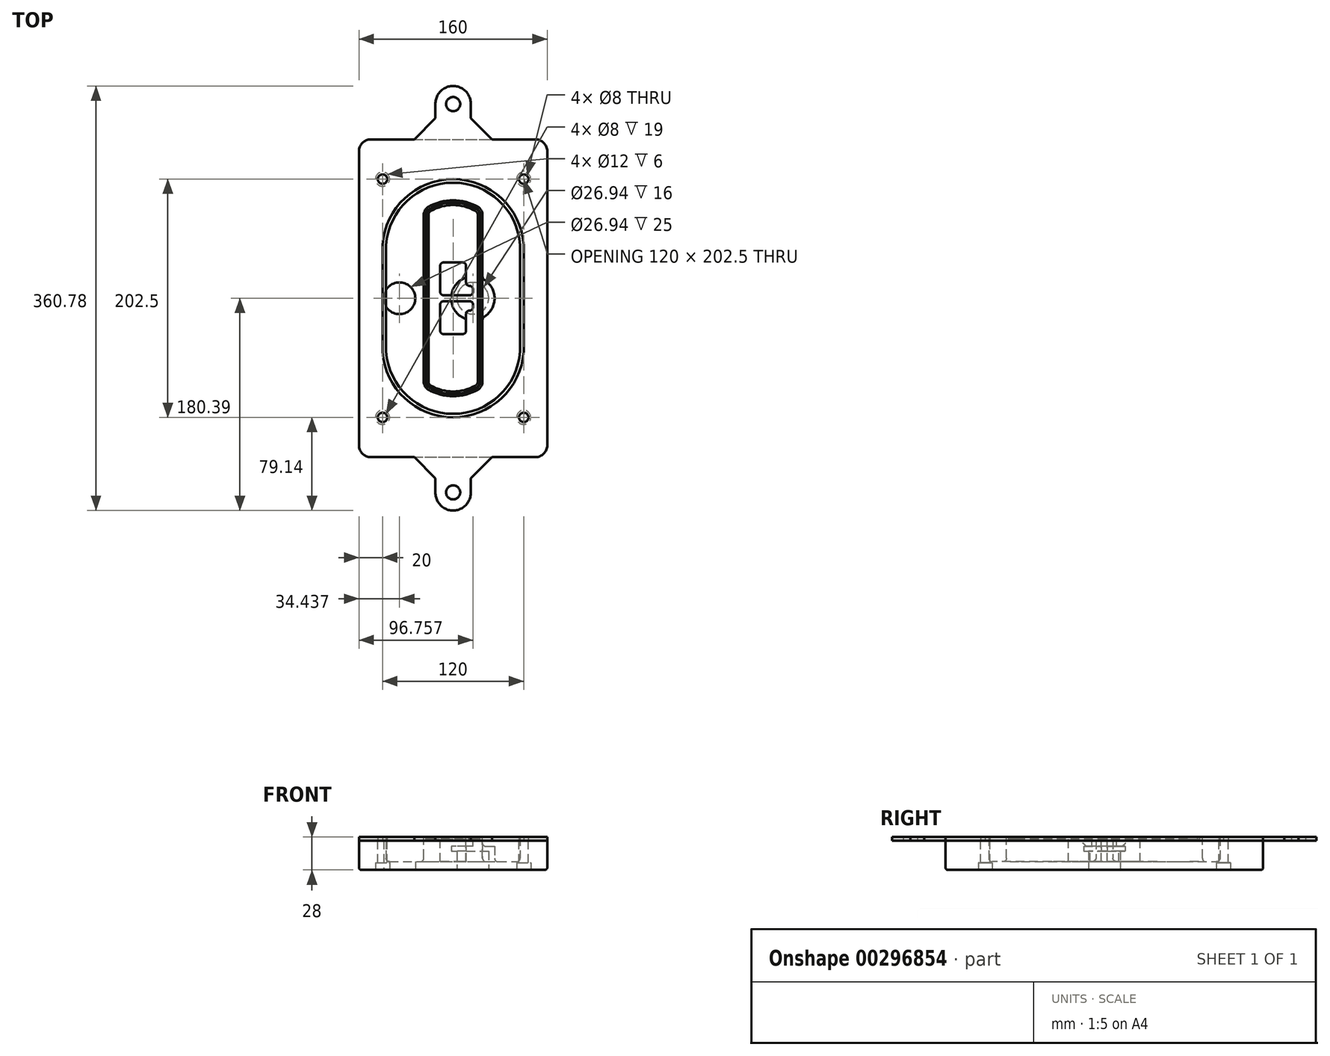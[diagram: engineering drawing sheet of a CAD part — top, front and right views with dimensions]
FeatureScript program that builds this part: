
annotation { "Feature Type Name" : "Feature", "Feature Type Description" : "" }
export const myFeature = defineFeature(function(context is Context, id is Id, definition is map)
    precondition{}
    {
        {
            var Q0;
            Q0=qCreatedBy(makeId("Top.planeOp"),FACE);
            var sketch = newSketch(context, id + "F0", { "sketchPlane" : qUnion([Q0])});
            skPoint(sketch, "E0.rect.middle", {"position": v(0, 0) * mm});
            skLineSegment(sketch, "E1.bottom", {"start": v(-70, -135) * mm, "end": v(70, -135) * mm});
            skLineSegment(sketch, "E1.top", {"start": v(-70, 135) * mm, "end": v(70, 135) * mm});
            skLineSegment(sketch, "E1.left", {"start": v(-80, -125) * mm, "end": v(-80, 125) * mm});
            skLineSegment(sketch, "E1.right", {"start": v(80, -125) * mm, "end": v(80, 125) * mm});
            skLineSegment(sketch, "E2", {"start": v(-80, 135) * mm, "end": v(80, -135) * mm, "construction": true});
            skLineSegment(sketch, "E3", {"start": v(80, 135) * mm, "end": v(-80, -135) * mm, "construction": true});
            skCircle(sketch, "E4", {"center": v(-60, 101.25) * mm, "radius": 4 * mm});
            skCircle(sketch, "E5", {"center": v(60, 101.25) * mm, "radius": 4 * mm});
            skCircle(sketch, "E6", {"center": v(60, -101.25) * mm, "radius": 4 * mm});
            skCircle(sketch, "E7", {"center": v(-60, -101.25) * mm, "radius": 4 * mm});
            skLineSegment(sketch, "E8", {"start": v(-60, 101.25) * mm, "end": v(60, 101.25) * mm, "construction": true});
            skLineSegment(sketch, "E9", {"start": v(60, 101.25) * mm, "end": v(60, -101.25) * mm, "construction": true});
            skLineSegment(sketch, "E10", {"start": v(60, -101.25) * mm, "end": v(-60, -101.25) * mm, "construction": true});
            skLineSegment(sketch, "E11", {"start": v(-60, -101.25) * mm, "end": v(-60, 101.25) * mm, "construction": true});
            skLineSegment(sketch, "E12", {"start": v(-60, 44.66) * mm, "end": v(-60, -44.66) * mm});
            skLineSegment(sketch, "E13", {"start": v(60, 44.66) * mm, "end": v(60, -44.66) * mm});
            skArc(sketch, "E14", {"start": v(59.98, 45.37) * mm, "mid": v(0, 101.25) * mm, "end": v(-59.98, 45.37) * mm});
            skArc(sketch, "E15", {"start": v(-59.98, -45.37) * mm, "mid": v(0, -101.25) * mm, "end": v(59.98, -45.37) * mm});
            skLineSegment(sketch, "E16", {"start": v(-60, 0) * mm, "end": v(60, 0) * mm, "construction": true});
            skPoint(sketch, "E17.visualSharp", {"position": v(-60, -45) * mm});
            skArc(sketch, "E17.filletArc", {"start": v(-60, -44.66) * mm, "mid": v(-60, -45.02) * mm, "end": v(-59.98, -45.37) * mm});
            skPoint(sketch, "E18.visualSharp", {"position": v(-60, 45) * mm});
            skArc(sketch, "E18.filletArc", {"start": v(-59.98, 45.37) * mm, "mid": v(-60, 45.02) * mm, "end": v(-60, 44.66) * mm});
            skPoint(sketch, "E19.visualSharp", {"position": v(60, 45) * mm});
            skArc(sketch, "E19.filletArc", {"start": v(60, 44.66) * mm, "mid": v(60, 45.02) * mm, "end": v(59.98, 45.37) * mm});
            skPoint(sketch, "E20.visualSharp", {"position": v(60, -45) * mm});
            skArc(sketch, "E20.filletArc", {"start": v(59.98, -45.37) * mm, "mid": v(60, -45.02) * mm, "end": v(60, -44.66) * mm});
            skPoint(sketch, "E21.visualSharp", {"position": v(-80, 135) * mm});
            skArc(sketch, "E21.filletArc", {"start": v(-70, 135) * mm, "mid": v(-77.07, 132.07) * mm, "end": v(-80, 125) * mm});
            skPoint(sketch, "E22.visualSharp", {"position": v(80, 135) * mm});
            skArc(sketch, "E22.filletArc", {"start": v(80, 125) * mm, "mid": v(77.07, 132.07) * mm, "end": v(70, 135) * mm});
            skPoint(sketch, "E23.visualSharp", {"position": v(80, -135) * mm});
            skArc(sketch, "E23.filletArc", {"start": v(70, -135) * mm, "mid": v(77.07, -132.07) * mm, "end": v(80, -125) * mm});
            skPoint(sketch, "E24.visualSharp", {"position": v(-80, -135) * mm});
            skArc(sketch, "E24.filletArc", {"start": v(-80, -125) * mm, "mid": v(-77.07, -132.07) * mm, "end": v(-70, -135) * mm});
            skArc(sketch, "E25.0", {"start": v(57, 44.66) * mm, "mid": v(57, 44.9) * mm, "end": v(56.98, 45.16) * mm});
            skLineSegment(sketch, "E25.1", {"start": v(57, 44.66) * mm, "end": v(57, -44.66) * mm});
            skArc(sketch, "E25.2", {"start": v(56.98, -45.16) * mm, "mid": v(57, -44.9) * mm, "end": v(57, -44.66) * mm});
            skArc(sketch, "E25.3", {"start": v(-56.98, -45.16) * mm, "mid": v(0, -98.25) * mm, "end": v(56.98, -45.16) * mm});
            skArc(sketch, "E25.4", {"start": v(-57, -44.66) * mm, "mid": v(-57, -44.9) * mm, "end": v(-56.98, -45.16) * mm});
            skArc(sketch, "E25.5", {"start": v(56.98, 45.16) * mm, "mid": v(0, 98.25) * mm, "end": v(-56.98, 45.16) * mm});
            skLineSegment(sketch, "E25.6", {"start": v(-57, 44.66) * mm, "end": v(-57, -44.66) * mm});
            skArc(sketch, "E25.7", {"start": v(-56.98, 45.16) * mm, "mid": v(-57, 44.9) * mm, "end": v(-57, 44.66) * mm});
            skArc(sketch, "E26.0", {"start": v(-63.97, 45.65) * mm, "mid": v(-64, 45.16) * mm, "end": v(-64, 44.66) * mm});
            skArc(sketch, "E26.1", {"start": v(63.97, 45.65) * mm, "mid": v(0, 105.25) * mm, "end": v(-63.97, 45.65) * mm});
            skArc(sketch, "E26.2", {"start": v(64, 44.66) * mm, "mid": v(64, 45.16) * mm, "end": v(63.97, 45.65) * mm});
            skLineSegment(sketch, "E26.3", {"start": v(64, 44.66) * mm, "end": v(64, -44.66) * mm});
            skArc(sketch, "E26.4", {"start": v(63.97, -45.65) * mm, "mid": v(64, -45.16) * mm, "end": v(64, -44.66) * mm});
            skLineSegment(sketch, "E26.5", {"start": v(-64, 44.66) * mm, "end": v(-64, -44.66) * mm});
            skArc(sketch, "E26.6", {"start": v(-63.97, -45.65) * mm, "mid": v(0, -105.25) * mm, "end": v(63.97, -45.65) * mm});
            skArc(sketch, "E26.7", {"start": v(-64, -44.66) * mm, "mid": v(-64, -45.16) * mm, "end": v(-63.97, -45.65) * mm});
            skSolve(sketch);
        }
        {
            var Q0;
            Q0=makeQuery(id+"F0.imprint","IMPRINT",FACE,{"disambiguationData":[TD([[makeQuery(id+"F0.imprint","IMPRINT",EDGE,{"derivedFrom":sQuery(id+"F0.wireOp",EDGE,"E1.bottom")}),1.0]])]});
            var Q1;
            Q1=makeQuery(id+"F0.imprint","IMPRINT",FACE,{"disambiguationData":[TD([[makeQuery(id+"F0.imprint","IMPRINT",EDGE,{"derivedFrom":sQuery(id+"F0.wireOp",EDGE,"E12")}),1.0]])]});
            var Q2;
            Q2=makeQuery(id+"F0.imprint","IMPRINT",FACE,{"disambiguationData":[TD([[makeQuery(id+"F0.imprint","IMPRINT",EDGE,{"derivedFrom":sQuery(id+"F0.wireOp",EDGE,"E25.0")}),1.0]])]});
            var Q3;
            Q3=makeQuery(id+"F0.imprint","IMPRINT",FACE,{"disambiguationData":[TD([[makeQuery(id+"F0.imprint","IMPRINT",EDGE,{"derivedFrom":sQuery(id+"F0.wireOp",EDGE,"E12")}),-1.0]])]});
            extrude(context, id + "F1", {"entities" : qUnion([Q0, Q1, Q2, Q3]), "oppositeDirection" : true, "depth" : 25 * mm});
        }
        {
            var Q0;
            Q0=makeQuery(id+"F0.imprint","IMPRINT",FACE,{"disambiguationData":[TD([[makeQuery(id+"F0.imprint","IMPRINT",EDGE,{"derivedFrom":sQuery(id+"F0.wireOp",EDGE,"E12")}),1.0]])]});
            extrude(context, id + "F2", {"entities" : qUnion([Q0]), "operationType" : NewBodyOperationType.ADD, "depth" : 3 * mm});
        }
        {
            var Q0;
            Q0=makeQuery(id+"F0.imprint","IMPRINT",FACE,{"disambiguationData":[TD([[makeQuery(id+"F0.imprint","IMPRINT",EDGE,{"derivedFrom":sQuery(id+"F0.wireOp",EDGE,"E25.0")}),1.0]])]});
            extrude(context, id + "F3", {"entities" : qUnion([Q0]), "operationType" : NewBodyOperationType.REMOVE, "oppositeDirection" : true, "depth" : 18 * mm});
        }
        {
            var Q0;
            Q0=makeQuery(id+"F2.opExtrude","CAP_FACE",FACE,{"disambiguationData":[OSD([sQuery(id+"F0.wireOp",EDGE,"E12"),sQuery(id+"F0.wireOp",EDGE,"E13"),sQuery(id+"F0.wireOp",EDGE,"E14"),sQuery(id+"F0.wireOp",EDGE,"E15"),sQuery(id+"F0.wireOp",EDGE,"E17.filletArc"),sQuery(id+"F0.wireOp",EDGE,"E18.filletArc"),sQuery(id+"F0.wireOp",EDGE,"E19.filletArc"),sQuery(id+"F0.wireOp",EDGE,"E20.filletArc"),sQuery(id+"F0.wireOp",EDGE,"E25.0"),sQuery(id+"F0.wireOp",EDGE,"E25.1"),sQuery(id+"F0.wireOp",EDGE,"E25.2"),sQuery(id+"F0.wireOp",EDGE,"E25.3"),sQuery(id+"F0.wireOp",EDGE,"E25.4"),sQuery(id+"F0.wireOp",EDGE,"E25.5"),sQuery(id+"F0.wireOp",EDGE,"E25.6"),sQuery(id+"F0.wireOp",EDGE,"E25.7")])],"isStart":false});
            var sketch = newSketch(context, id + "F4", { "sketchPlane" : qUnion([Q0])});
            skArc(sketch, "E27.0", {"start": v(-20.99, -77.65) * mm, "mid": v(0, -83.25) * mm, "end": v(20.99, -77.65) * mm});
            skArc(sketch, "E28.0", {"start": v(20.99, 77.65) * mm, "mid": v(0, 83.25) * mm, "end": v(-20.99, 77.65) * mm});
            skLineSegment(sketch, "E29", {"start": v(-25, 70.71) * mm, "end": v(-25, -70.71) * mm});
            skLineSegment(sketch, "E30", {"start": v(25, 70.71) * mm, "end": v(25, -70.71) * mm});
            skLineSegment(sketch, "E31", {"start": v(-25, 75.03) * mm, "end": v(25, 75.03) * mm, "construction": true});
            skLineSegment(sketch, "E32", {"start": v(-25, -75.03) * mm, "end": v(25, -75.03) * mm, "construction": true});
            skPoint(sketch, "E33.visualSharp", {"position": v(-25, 75.03) * mm});
            skArc(sketch, "E33.filletArc", {"start": v(-20.99, 77.65) * mm, "mid": v(-23.92, 74.72) * mm, "end": v(-25, 70.71) * mm});
            skPoint(sketch, "E34.visualSharp", {"position": v(25, 75.03) * mm});
            skArc(sketch, "E34.filletArc", {"start": v(25, 70.71) * mm, "mid": v(23.92, 74.72) * mm, "end": v(20.99, 77.65) * mm});
            skPoint(sketch, "E35.visualSharp", {"position": v(25, -75.03) * mm});
            skArc(sketch, "E35.filletArc", {"start": v(20.99, -77.65) * mm, "mid": v(23.92, -74.72) * mm, "end": v(25, -70.71) * mm});
            skPoint(sketch, "E36.visualSharp", {"position": v(-25, -75.03) * mm});
            skArc(sketch, "E36.filletArc", {"start": v(-25, -70.71) * mm, "mid": v(-23.92, -74.72) * mm, "end": v(-20.99, -77.65) * mm});
            skArc(sketch, "E37.0", {"start": v(56.98, 45.16) * mm, "mid": v(0, 98.25) * mm, "end": v(-56.98, 45.16) * mm});
            skArc(sketch, "E37.1", {"start": v(-56.98, 45.16) * mm, "mid": v(-57, 44.9) * mm, "end": v(-57, 44.66) * mm});
            skLineSegment(sketch, "E37.2", {"start": v(-57, 44.66) * mm, "end": v(-57, -44.66) * mm});
            skArc(sketch, "E37.3", {"start": v(-57, -44.66) * mm, "mid": v(-57, -44.9) * mm, "end": v(-56.98, -45.16) * mm});
            skArc(sketch, "E37.4", {"start": v(-56.98, -45.16) * mm, "mid": v(0, -98.25) * mm, "end": v(56.98, -45.16) * mm});
            skArc(sketch, "E37.5", {"start": v(56.98, -45.16) * mm, "mid": v(57, -44.9) * mm, "end": v(57, -44.66) * mm});
            skLineSegment(sketch, "E37.6", {"start": v(57, 44.66) * mm, "end": v(57, -44.66) * mm});
            skArc(sketch, "E37.7", {"start": v(57, 44.66) * mm, "mid": v(57, 44.9) * mm, "end": v(56.98, 45.16) * mm});
            skLineSegment(sketch, "E38.0", {"start": v(23, 70.71) * mm, "end": v(23, -70.71) * mm});
            skArc(sketch, "E38.1", {"start": v(19.99, -75.92) * mm, "mid": v(22.2, -73.72) * mm, "end": v(23, -70.71) * mm});
            skArc(sketch, "E38.2", {"start": v(-19.99, -75.92) * mm, "mid": v(0, -81.25) * mm, "end": v(19.99, -75.92) * mm});
            skArc(sketch, "E38.3", {"start": v(-23, -70.71) * mm, "mid": v(-22.2, -73.72) * mm, "end": v(-19.99, -75.92) * mm});
            skLineSegment(sketch, "E38.4", {"start": v(-23, 70.71) * mm, "end": v(-23, -70.71) * mm});
            skArc(sketch, "E38.5", {"start": v(23, 70.71) * mm, "mid": v(22.2, 73.72) * mm, "end": v(19.99, 75.92) * mm});
            skArc(sketch, "E38.6", {"start": v(-19.99, 75.92) * mm, "mid": v(-22.2, 73.72) * mm, "end": v(-23, 70.71) * mm});
            skArc(sketch, "E38.7", {"start": v(19.99, 75.92) * mm, "mid": v(0, 81.25) * mm, "end": v(-19.99, 75.92) * mm});
            skArc(sketch, "E39.0", {"start": v(21, 70.71) * mm, "mid": v(20.46, 72.72) * mm, "end": v(19, 74.18) * mm});
            skLineSegment(sketch, "E39.1", {"start": v(21, 70.71) * mm, "end": v(21, -70.71) * mm});
            skArc(sketch, "E39.2", {"start": v(19, -74.18) * mm, "mid": v(20.46, -72.72) * mm, "end": v(21, -70.71) * mm});
            skArc(sketch, "E39.3", {"start": v(-19, -74.18) * mm, "mid": v(0, -79.25) * mm, "end": v(19, -74.18) * mm});
            skArc(sketch, "E39.4", {"start": v(-21, -70.71) * mm, "mid": v(-20.46, -72.72) * mm, "end": v(-19, -74.18) * mm});
            skArc(sketch, "E39.5", {"start": v(19, 74.18) * mm, "mid": v(0, 79.25) * mm, "end": v(-19, 74.18) * mm});
            skLineSegment(sketch, "E39.6", {"start": v(-21, 70.71) * mm, "end": v(-21, -70.71) * mm});
            skArc(sketch, "E39.7", {"start": v(-19, 74.18) * mm, "mid": v(-20.46, 72.72) * mm, "end": v(-21, 70.71) * mm});
            skLineSegment(sketch, "E40", {"start": v(-25, 0) * mm, "end": v(25, 0) * mm, "construction": true});
            skLineSegment(sketch, "E41", {"start": v(-11, 5.5) * mm, "end": v(-11, 27.5) * mm});
            skLineSegment(sketch, "E42", {"start": v(-8, 30.5) * mm, "end": v(8, 30.5) * mm});
            skLineSegment(sketch, "E43", {"start": v(11, 27.5) * mm, "end": v(11, 13.5) * mm});
            skLineSegment(sketch, "E44", {"start": v(14, 10.5) * mm, "end": v(14, 10.5) * mm});
            skLineSegment(sketch, "E45", {"start": v(17, 7.5) * mm, "end": v(17, 5.5) * mm});
            skLineSegment(sketch, "E46", {"start": v(14, 2.5) * mm, "end": v(-8, 2.5) * mm});
            skPoint(sketch, "E47.visualSharp", {"position": v(-11, 30.5) * mm});
            skArc(sketch, "E47.filletArc", {"start": v(-8, 30.5) * mm, "mid": v(-10.12, 29.62) * mm, "end": v(-11, 27.5) * mm});
            skPoint(sketch, "E48.visualSharp", {"position": v(11, 30.5) * mm});
            skArc(sketch, "E48.filletArc", {"start": v(11, 27.5) * mm, "mid": v(10.12, 29.62) * mm, "end": v(8, 30.5) * mm});
            skPoint(sketch, "E49.visualSharp", {"position": v(11, 10.5) * mm});
            skArc(sketch, "E49.filletArc", {"start": v(11, 13.5) * mm, "mid": v(11.88, 11.38) * mm, "end": v(14, 10.5) * mm});
            skPoint(sketch, "E50.visualSharp", {"position": v(17, 10.5) * mm});
            skArc(sketch, "E50.filletArc", {"start": v(17, 7.5) * mm, "mid": v(16.12, 9.62) * mm, "end": v(14, 10.5) * mm});
            skPoint(sketch, "E51.visualSharp", {"position": v(17, 2.5) * mm});
            skArc(sketch, "E51.filletArc", {"start": v(14, 2.5) * mm, "mid": v(16.12, 3.38) * mm, "end": v(17, 5.5) * mm});
            skPoint(sketch, "E52.visualSharp", {"position": v(-11, 2.5) * mm});
            skArc(sketch, "E52.filletArc", {"start": v(-11, 5.5) * mm, "mid": v(-10.12, 3.38) * mm, "end": v(-8, 2.5) * mm});
            skLineSegment(sketch, "E53.0.MirrorCS", {"start": v(14, -2.5) * mm, "end": v(-8, -2.5) * mm});
            skArc(sketch, "E54.0.MirrorCS", {"start": v(-11, -5.5) * mm, "mid": v(-10.12, -3.38) * mm, "end": v(-8, -2.5) * mm});
            skLineSegment(sketch, "E55.0.MirrorCS", {"start": v(-11, -5.5) * mm, "end": v(-11, -27.5) * mm});
            skArc(sketch, "E56.0.MirrorCS", {"start": v(-8, -30.5) * mm, "mid": v(-10.12, -29.62) * mm, "end": v(-11, -27.5) * mm});
            skLineSegment(sketch, "E57.0.MirrorCS", {"start": v(-8, -30.5) * mm, "end": v(8, -30.5) * mm});
            skArc(sketch, "E58.0.MirrorCS", {"start": v(11, -27.5) * mm, "mid": v(10.12, -29.62) * mm, "end": v(8, -30.5) * mm});
            skLineSegment(sketch, "E59.0.MirrorCS", {"start": v(11, -27.5) * mm, "end": v(11, -13.5) * mm});
            skArc(sketch, "E60.0.MirrorCS", {"start": v(11, -13.5) * mm, "mid": v(11.88, -11.38) * mm, "end": v(14, -10.5) * mm});
            skArc(sketch, "E61.0.MirrorCS", {"start": v(17, -7.5) * mm, "mid": v(16.12, -9.62) * mm, "end": v(14, -10.5) * mm});
            skLineSegment(sketch, "E62.0.MirrorCS", {"start": v(17, -7.5) * mm, "end": v(17, -5.5) * mm});
            skArc(sketch, "E63.0.MirrorCS", {"start": v(14, -2.5) * mm, "mid": v(16.12, -3.38) * mm, "end": v(17, -5.5) * mm});
            skSolve(sketch);
        }
        {
            var Q0;
            Q0=makeQuery(id+"F4.imprint","IMPRINT",FACE,{"disambiguationData":[TD([[makeQuery(id+"F4.imprint","IMPRINT",EDGE,{"derivedFrom":sQuery(id+"F4.wireOp",EDGE,"E27.0")}),1.0]])]});
            var Q1;
            Q1=makeQuery(id+"F4.imprint","IMPRINT",FACE,{"disambiguationData":[TD([[makeQuery(id+"F4.imprint","IMPRINT",EDGE,{"derivedFrom":sQuery(id+"F4.wireOp",EDGE,"E38.0")}),-1.0]])]});
            var Q2;
            Q2=makeQuery(id+"F4.imprint","IMPRINT",FACE,{"disambiguationData":[TD([[makeQuery(id+"F4.imprint","IMPRINT",EDGE,{"derivedFrom":sQuery(id+"F4.wireOp",EDGE,"E39.0")}),1.0]])]});
            extrude(context, id + "F5", {"entities" : qUnion([Q0, Q1, Q2]), "operationType" : NewBodyOperationType.ADD, "endBound" : BoundingType.UP_TO_NEXT, "oppositeDirection" : true, "depth" : 25 * mm});
        }
        {
            var Q0;
            Q0=makeQuery(id+"F4.imprint","IMPRINT",FACE,{"disambiguationData":[TD([[makeQuery(id+"F4.imprint","IMPRINT",EDGE,{"derivedFrom":sQuery(id+"F4.wireOp",EDGE,"E38.0")}),-1.0]])]});
            extrude(context, id + "F6", {"entities" : qUnion([Q0]), "operationType" : NewBodyOperationType.REMOVE, "oppositeDirection" : true, "depth" : 2 * mm});
        }
        {
            var Q0;
            Q0=makeQuery(id+"F1.opExtrude","CAP_FACE",FACE,{"disambiguationData":[OSD([sQuery(id+"F0.wireOp",EDGE,"E1.bottom"),sQuery(id+"F0.wireOp",EDGE,"E1.top"),sQuery(id+"F0.wireOp",EDGE,"E1.left"),sQuery(id+"F0.wireOp",EDGE,"E1.right"),sQuery(id+"F0.wireOp",EDGE,"E4"),sQuery(id+"F0.wireOp",EDGE,"E5"),sQuery(id+"F0.wireOp",EDGE,"E6"),sQuery(id+"F0.wireOp",EDGE,"E7"),sQuery(id+"F0.wireOp",EDGE,"E21.filletArc"),sQuery(id+"F0.wireOp",EDGE,"E22.filletArc"),sQuery(id+"F0.wireOp",EDGE,"E23.filletArc"),sQuery(id+"F0.wireOp",EDGE,"E24.filletArc")])],"isStart":false});
            var sketch = newSketch(context, id + "F7", { "sketchPlane" : qUnion([Q0])});
            skCircle(sketch, "E64", {"center": v(16.76, 0) * mm, "radius": 13.47 * mm});
            skCircle(sketch, "E65", {"center": v(-45.56, 0) * mm, "radius": 13.47 * mm});
            skLineSegment(sketch, "E66", {"start": v(80, 0) * mm, "end": v(-80, 0) * mm});
            skCircle(sketch, "E67", {"center": v(16.76, 0) * mm, "radius": 18.47 * mm});
            skCircle(sketch, "E68", {"center": v(60, -101.25) * mm, "radius": 6 * mm});
            skCircle(sketch, "E69", {"center": v(-60, -101.25) * mm, "radius": 6 * mm});
            skCircle(sketch, "E70", {"center": v(-60, 101.25) * mm, "radius": 6 * mm});
            skCircle(sketch, "E71", {"center": v(60, 101.25) * mm, "radius": 6 * mm});
            skSolve(sketch);
        }
        {
            var Q0;
            {var subQ1=sQuery(id+"F7.wireOp",EDGE,"E66");var subQ4=sQuery(id+"F7.wireOp",EDGE,"E64");var subQ6=makeQuery(id+"F7.imprint","INTERSECT",VERTEX,{"disambiguationData":[OD(0.0)],"derivedFrom":[subQ4,subQ1]});Q0=makeQuery(id+"F7.imprint","IMPRINT",FACE,{"disambiguationData":[TD([[makeQuery(id+"F7.imprint","IMPRINT",EDGE,{"disambiguationData":[TD([[subQ6,-1.0]])],"derivedFrom":subQ4}),-1.0]])]});}
            var Q1;
            {var subQ0=sQuery(id+"F7.wireOp",EDGE,"E66");var subQ1=sQuery(id+"F7.wireOp",EDGE,"E64");var subQ3=makeQuery(id+"F7.imprint","INTERSECT",VERTEX,{"disambiguationData":[OD(0.0)],"derivedFrom":[subQ1,subQ0]});Q1=makeQuery(id+"F7.imprint","IMPRINT",FACE,{"disambiguationData":[TD([[makeQuery(id+"F7.imprint","IMPRINT",EDGE,{"disambiguationData":[TD([[subQ3,-1.0]])],"derivedFrom":subQ1}),1.0]])]});}
            var Q2;
            {var subQ0=sQuery(id+"F7.wireOp",EDGE,"E66");var subQ1=sQuery(id+"F7.wireOp",EDGE,"E64");var subQ3=makeQuery(id+"F7.imprint","INTERSECT",VERTEX,{"disambiguationData":[OD(0.0)],"derivedFrom":[subQ1,subQ0]});Q2=makeQuery(id+"F7.imprint","IMPRINT",FACE,{"disambiguationData":[TD([[makeQuery(id+"F7.imprint","IMPRINT",EDGE,{"disambiguationData":[TD([[subQ3,1.0]])],"derivedFrom":subQ1}),1.0]])]});}
            var Q3;
            {var subQ1=sQuery(id+"F7.wireOp",EDGE,"E66");var subQ4=sQuery(id+"F7.wireOp",EDGE,"E64");var subQ6=makeQuery(id+"F7.imprint","INTERSECT",VERTEX,{"disambiguationData":[OD(0.0)],"derivedFrom":[subQ4,subQ1]});Q3=makeQuery(id+"F7.imprint","IMPRINT",FACE,{"disambiguationData":[TD([[makeQuery(id+"F7.imprint","IMPRINT",EDGE,{"disambiguationData":[TD([[subQ6,1.0]])],"derivedFrom":subQ4}),-1.0]])]});}
            extrude(context, id + "F8", {"entities" : qUnion([Q0, Q1, Q2, Q3]), "operationType" : NewBodyOperationType.ADD, "oppositeDirection" : true, "depth" : 20 * mm});
        }
        {
            var Q0;
            {var subQ0=sQuery(id+"F7.wireOp",EDGE,"E66");var subQ1=sQuery(id+"F7.wireOp",EDGE,"E64");var subQ3=makeQuery(id+"F7.imprint","INTERSECT",VERTEX,{"disambiguationData":[OD(0.0)],"derivedFrom":[subQ1,subQ0]});Q0=makeQuery(id+"F7.imprint","IMPRINT",FACE,{"disambiguationData":[TD([[makeQuery(id+"F7.imprint","IMPRINT",EDGE,{"disambiguationData":[TD([[subQ3,-1.0]])],"derivedFrom":subQ1}),1.0]])]});}
            var Q1;
            {var subQ0=sQuery(id+"F7.wireOp",EDGE,"E66");var subQ1=sQuery(id+"F7.wireOp",EDGE,"E64");var subQ3=makeQuery(id+"F7.imprint","INTERSECT",VERTEX,{"disambiguationData":[OD(0.0)],"derivedFrom":[subQ1,subQ0]});Q1=makeQuery(id+"F7.imprint","IMPRINT",FACE,{"disambiguationData":[TD([[makeQuery(id+"F7.imprint","IMPRINT",EDGE,{"disambiguationData":[TD([[subQ3,1.0]])],"derivedFrom":subQ1}),1.0]])]});}
            extrude(context, id + "F9", {"entities" : qUnion([Q0, Q1]), "operationType" : NewBodyOperationType.REMOVE, "oppositeDirection" : true, "depth" : 16 * mm});
        }
        {
            var Q0;
            {var subQ0=sQuery(id+"F7.wireOp",EDGE,"E66");var subQ1=sQuery(id+"F7.wireOp",EDGE,"E65");var subQ3=makeQuery(id+"F7.imprint","INTERSECT",VERTEX,{"disambiguationData":[OD(0.0)],"derivedFrom":[subQ1,subQ0]});Q0=makeQuery(id+"F7.imprint","IMPRINT",FACE,{"disambiguationData":[TD([[makeQuery(id+"F7.imprint","IMPRINT",EDGE,{"disambiguationData":[TD([[subQ3,-1.0]])],"derivedFrom":subQ1}),1.0]])]});}
            var Q1;
            {var subQ0=sQuery(id+"F7.wireOp",EDGE,"E66");var subQ1=sQuery(id+"F7.wireOp",EDGE,"E65");var subQ3=makeQuery(id+"F7.imprint","INTERSECT",VERTEX,{"disambiguationData":[OD(0.0)],"derivedFrom":[subQ1,subQ0]});Q1=makeQuery(id+"F7.imprint","IMPRINT",FACE,{"disambiguationData":[TD([[makeQuery(id+"F7.imprint","IMPRINT",EDGE,{"disambiguationData":[TD([[subQ3,1.0]])],"derivedFrom":subQ1}),1.0]])]});}
            extrude(context, id + "F10", {"entities" : qUnion([Q0, Q1]), "operationType" : NewBodyOperationType.REMOVE, "oppositeDirection" : true, "depth" : 25 * mm});
        }
        {
            var Q0;
            Q0=makeQuery(id+"F7.imprint","IMPRINT",FACE,{"disambiguationData":[TD([[makeQuery(id+"F7.imprint","IMPRINT",EDGE,{"derivedFrom":sQuery(id+"F7.wireOp",EDGE,"E68")}),1.0]])]});
            var Q1;
            Q1=makeQuery(id+"F7.imprint","IMPRINT",FACE,{"disambiguationData":[TD([[makeQuery(id+"F7.imprint","IMPRINT",EDGE,{"derivedFrom":makeQuery(id+"F1.opExtrude","CAP_EDGE",EDGE,{"disambiguationData":[OSD([sQuery(id+"F0.wireOp",EDGE,"E5")])],"isStart":false})}),-1.0]])]});
            var Q2;
            Q2=makeQuery(id+"F7.imprint","IMPRINT",FACE,{"disambiguationData":[TD([[makeQuery(id+"F7.imprint","IMPRINT",EDGE,{"derivedFrom":sQuery(id+"F7.wireOp",EDGE,"E69")}),1.0]])]});
            var Q3;
            Q3=makeQuery(id+"F7.imprint","IMPRINT",FACE,{"disambiguationData":[TD([[makeQuery(id+"F7.imprint","IMPRINT",EDGE,{"derivedFrom":makeQuery(id+"F1.opExtrude","CAP_EDGE",EDGE,{"disambiguationData":[OSD([sQuery(id+"F0.wireOp",EDGE,"E4")])],"isStart":false})}),-1.0]])]});
            var Q4;
            Q4=makeQuery(id+"F7.imprint","IMPRINT",FACE,{"disambiguationData":[TD([[makeQuery(id+"F7.imprint","IMPRINT",EDGE,{"derivedFrom":sQuery(id+"F7.wireOp",EDGE,"E70")}),1.0]])]});
            var Q5;
            Q5=makeQuery(id+"F7.imprint","IMPRINT",FACE,{"disambiguationData":[TD([[makeQuery(id+"F7.imprint","IMPRINT",EDGE,{"derivedFrom":makeQuery(id+"F1.opExtrude","CAP_EDGE",EDGE,{"disambiguationData":[OSD([sQuery(id+"F0.wireOp",EDGE,"E7")])],"isStart":false})}),-1.0]])]});
            var Q6;
            Q6=makeQuery(id+"F7.imprint","IMPRINT",FACE,{"disambiguationData":[TD([[makeQuery(id+"F7.imprint","IMPRINT",EDGE,{"derivedFrom":sQuery(id+"F7.wireOp",EDGE,"E71")}),1.0]])]});
            var Q7;
            Q7=makeQuery(id+"F7.imprint","IMPRINT",FACE,{"disambiguationData":[TD([[makeQuery(id+"F7.imprint","IMPRINT",EDGE,{"derivedFrom":makeQuery(id+"F1.opExtrude","CAP_EDGE",EDGE,{"disambiguationData":[OSD([sQuery(id+"F0.wireOp",EDGE,"E6")])],"isStart":false})}),-1.0]])]});
            extrude(context, id + "F11", {"entities" : qUnion([Q0, Q1, Q2, Q3, Q4, Q5, Q6, Q7]), "operationType" : NewBodyOperationType.REMOVE, "oppositeDirection" : true, "depth" : 6 * mm});
        }
        {
            var Q0;
            Q0=makeQuery(id+"F9.boolean.opBoolean","COPY",FACE,{"derivedFrom":makeQuery(id+"F9.opExtrude","CAP_FACE",FACE,{"disambiguationData":[OSD([sQuery(id+"F7.wireOp",EDGE,"E64")])],"isStart":false})});
            var sketch = newSketch(context, id + "F12", { "sketchPlane" : qUnion([Q0])});
            skArc(sketch, "E72.0", {"start": v(11, 17.55) * mm, "mid": v(2.57, 11.82) * mm, "end": v(-1.54, 2.5) * mm});
            skArc(sketch, "E72.1", {"start": v(-1.54, -2.5) * mm, "mid": v(2.57, -11.82) * mm, "end": v(11, -17.55) * mm});
            skLineSegment(sketch, "E73", {"start": v(-1.54, -2.5) * mm, "end": v(14, -2.5) * mm});
            skLineSegment(sketch, "E74.0", {"start": v(14, 2.5) * mm, "end": v(-1.54, 2.5) * mm});
            skArc(sketch, "E74.1", {"start": v(14, 2.5) * mm, "mid": v(16.12, 3.38) * mm, "end": v(17, 5.5) * mm});
            skLineSegment(sketch, "E74.2", {"start": v(17, 7.5) * mm, "end": v(17, 5.5) * mm});
            skArc(sketch, "E74.3", {"start": v(17, 7.5) * mm, "mid": v(16.12, 9.62) * mm, "end": v(14, 10.5) * mm});
            skArc(sketch, "E74.4", {"start": v(11, 13.5) * mm, "mid": v(11.88, 11.38) * mm, "end": v(14, 10.5) * mm});
            skLineSegment(sketch, "E74.5", {"start": v(11, 17.55) * mm, "end": v(11, 13.5) * mm});
            skLineSegment(sketch, "E74.7", {"start": v(14, -2.5) * mm, "end": v(-1.54, -2.5) * mm});
            skArc(sketch, "E74.8", {"start": v(14, -2.5) * mm, "mid": v(16.12, -3.38) * mm, "end": v(17, -5.5) * mm});
            skLineSegment(sketch, "E74.9", {"start": v(17, -7.5) * mm, "end": v(17, -5.5) * mm});
            skArc(sketch, "E74.10", {"start": v(17, -7.5) * mm, "mid": v(16.12, -9.62) * mm, "end": v(14, -10.5) * mm});
            skArc(sketch, "E74.11", {"start": v(11, -13.5) * mm, "mid": v(11.88, -11.38) * mm, "end": v(14, -10.5) * mm});
            skLineSegment(sketch, "E74.12", {"start": v(11, -17.55) * mm, "end": v(11, -13.5) * mm});
            skPoint(sketch, "E75.orphan", {"position": v(11, -27.5) * mm});
            skPoint(sketch, "E76.orphan", {"position": v(-8, -2.5) * mm});
            skPoint(sketch, "E77.orphan", {"position": v(-8, 2.5) * mm});
            skPoint(sketch, "E78.orphan", {"position": v(11, 27.5) * mm});
            skSolve(sketch);
        }
        {
            var Q0;
            {var subQ7=sQuery(id+"F12.wireOp",EDGE,"E72.0");var subQ14=sQuery(id+"F12.wireOp",EDGE,"E72.1");var subQ16=sQuery(id+"F12.wireOp",EDGE,"E74.1");var subQ18=sQuery(id+"F12.wireOp",EDGE,"E74.8");Q0=qUnion([makeQuery(id+"F12.imprint","IMPRINT",FACE,{"disambiguationData":[TD([[makeQuery(id+"F12.imprint","IMPRINT",EDGE,{"derivedFrom":subQ7}),1.0]])]}),makeQuery(id+"F12.imprint","IMPRINT",FACE,{"disambiguationData":[TD([[makeQuery(id+"F12.imprint","IMPRINT",EDGE,{"derivedFrom":subQ14}),1.0]])]}),makeQuery(id+"F12.imprint","IMPRINT",FACE,{"disambiguationData":[TD([[makeQuery(id+"F12.imprint","IMPRINT",EDGE,{"derivedFrom":subQ16}),1.0]])]}),makeQuery(id+"F12.imprint","IMPRINT",FACE,{"disambiguationData":[TD([[makeQuery(id+"F12.imprint","IMPRINT",EDGE,{"derivedFrom":subQ18}),-1.0]])]})]);}
            var Q1;
            Q1=makeQuery(id+"F5.boolean.opBoolean","SPLIT",FACE,{"disambiguationData":[TD([makeQuery(id+"F5.opExtrude","SWEPT_FACE",FACE,{"disambiguationData":[OSD([sQuery(id+"F4.wireOp",EDGE,"E41")])]})])],"derivedFrom":makeQuery(id+"F3.boolean.opBoolean","COPY",FACE,{"derivedFrom":makeQuery(id+"F3.opExtrude","CAP_FACE",FACE,{"disambiguationData":[OSD([sQuery(id+"F0.wireOp",EDGE,"E25.0"),sQuery(id+"F0.wireOp",EDGE,"E25.1"),sQuery(id+"F0.wireOp",EDGE,"E25.2"),sQuery(id+"F0.wireOp",EDGE,"E25.3"),sQuery(id+"F0.wireOp",EDGE,"E25.4"),sQuery(id+"F0.wireOp",EDGE,"E25.5"),sQuery(id+"F0.wireOp",EDGE,"E25.6"),sQuery(id+"F0.wireOp",EDGE,"E25.7")])],"isStart":false})})});
            extrude(context, id + "F13", {"entities" : qUnion([Q0]), "operationType" : NewBodyOperationType.REMOVE, "endBound" : BoundingType.UP_TO_SURFACE, "endBoundEntityFace" : qUnion([Q1]), "depth" : 25 * mm});
        }
        {
            var Q0;
            Q0=makeQuery(id+"F3.boolean.opBoolean","COPY",EDGE,{"derivedFrom":makeQuery(id+"F3.opExtrude","CAP_EDGE",EDGE,{"disambiguationData":[OSD([sQuery(id+"F0.wireOp",EDGE,"E25.6")])],"isStart":false})});
            var Q1;
            Q1=makeQuery(id+"F8.boolean.opBoolean","INTERSECT",EDGE,{"derivedFrom":[makeQuery(id+"F5.opExtrude","SWEPT_FACE",FACE,{"disambiguationData":[OSD([sQuery(id+"F4.wireOp",EDGE,"E30")])]}),makeQuery(id+"F8.opExtrude","CAP_FACE",FACE,{"disambiguationData":[OSD([sQuery(id+"F7.wireOp",EDGE,"E67")])],"isStart":false})]});
            var Q2;
            Q2=makeQuery(id+"F8.boolean.opBoolean","INTERSECT",EDGE,{"disambiguationData":[OD(1.0)],"derivedFrom":[makeQuery(id+"F5.opExtrude","SWEPT_FACE",FACE,{"disambiguationData":[OSD([sQuery(id+"F4.wireOp",EDGE,"E30")])]}),makeQuery(id+"F8.opExtrude","SWEPT_FACE",FACE,{"disambiguationData":[OSD([sQuery(id+"F7.wireOp",EDGE,"E67")])]})]});
            var Q3;
            {var subQ0=sQuery(id+"F4.wireOp",EDGE,"E30");Q3=makeQuery(id+"F8.boolean.opBoolean","SPLIT",EDGE,{"disambiguationData":[TD([makeQuery(id+"F5.opExtrude","SWEPT_FACE",FACE,{"disambiguationData":[OSD([sQuery(id+"F4.wireOp",EDGE,"E35.filletArc")])]})])],"derivedFrom":makeQuery(id+"F5.opExtrude","CAP_EDGE",EDGE,{"disambiguationData":[OSD([subQ0])],"isStart":false})});}
            var Q4;
            {var subQ0=sQuery(id+"F0.wireOp",EDGE,"E25.7");var subQ1=sQuery(id+"F0.wireOp",EDGE,"E25.1");var subQ2=sQuery(id+"F0.wireOp",EDGE,"E25.6");var subQ3=sQuery(id+"F0.wireOp",EDGE,"E25.5");var subQ4=sQuery(id+"F0.wireOp",EDGE,"E25.4");var subQ5=sQuery(id+"F0.wireOp",EDGE,"E25.0");var subQ6=sQuery(id+"F0.wireOp",EDGE,"E25.2");var subQ7=sQuery(id+"F0.wireOp",EDGE,"E25.3");Q4=makeQuery(id+"F8.boolean.opBoolean","INTERSECT",EDGE,{"derivedFrom":[makeQuery(id+"F5.boolean.opBoolean","SPLIT",FACE,{"disambiguationData":[TD([makeQuery(id+"F2.opExtrude","SWEPT_FACE",FACE,{"disambiguationData":[OSD([subQ5])]})])],"derivedFrom":makeQuery(id+"F3.boolean.opBoolean","COPY",FACE,{"derivedFrom":makeQuery(id+"F3.opExtrude","CAP_FACE",FACE,{"disambiguationData":[OSD([subQ5,subQ1,subQ6,subQ7,subQ4,subQ3,subQ2,subQ0])],"isStart":false})})}),makeQuery(id+"F8.opExtrude","SWEPT_FACE",FACE,{"disambiguationData":[OSD([sQuery(id+"F7.wireOp",EDGE,"E67")])]})]});}
            var Q5;
            Q5=makeQuery(id+"F8.boolean.opBoolean","INTERSECT",EDGE,{"disambiguationData":[OD(0.0)],"derivedFrom":[makeQuery(id+"F5.opExtrude","SWEPT_FACE",FACE,{"disambiguationData":[OSD([sQuery(id+"F4.wireOp",EDGE,"E30")])]}),makeQuery(id+"F8.opExtrude","SWEPT_FACE",FACE,{"disambiguationData":[OSD([sQuery(id+"F7.wireOp",EDGE,"E67")])]})]});
            fillet(context, id + "F14", {"entities" : qUnion([Q0, Q1, Q2, Q3, Q4, Q5]), "radius" : 3 * mm, "tangentPropagation" : true, "allowEdgeOverflow" : false});
        }
        {
            var Q0;
            Q0=makeQuery(id+"F1.opExtrude","CAP_EDGE",EDGE,{"disambiguationData":[OSD([sQuery(id+"F0.wireOp",EDGE,"E1.bottom")])],"isStart":false});
            fillet(context, id + "F15", {"entities" : qUnion([Q0]), "radius" : 2 * mm, "tangentPropagation" : true, "allowEdgeOverflow" : false});
        }
        {
            var Q0;
            {var subQ0=sQuery(id+"F0.wireOp",EDGE,"E21.filletArc");var subQ1=sQuery(id+"F0.wireOp",EDGE,"E7");var subQ2=sQuery(id+"F0.wireOp",EDGE,"E6");var subQ3=sQuery(id+"F0.wireOp",EDGE,"E5");var subQ4=sQuery(id+"F0.wireOp",EDGE,"E4");var subQ5=sQuery(id+"F0.wireOp",EDGE,"E22.filletArc");var subQ6=sQuery(id+"F0.wireOp",EDGE,"E1.bottom");var subQ7=sQuery(id+"F0.wireOp",EDGE,"E1.right");var subQ8=sQuery(id+"F0.wireOp",EDGE,"E1.top");var subQ9=sQuery(id+"F0.wireOp",EDGE,"E1.left");var subQ10=sQuery(id+"F0.wireOp",EDGE,"E23.filletArc");var subQ11=sQuery(id+"F0.wireOp",EDGE,"E24.filletArc");Q0=makeQuery(id+"F2.boolean.opBoolean","SPLIT",FACE,{"disambiguationData":[TD([makeQuery(id+"F1.opExtrude","SWEPT_FACE",FACE,{"disambiguationData":[OSD([subQ6])]})])],"derivedFrom":makeQuery(id+"F1.opExtrude","CAP_FACE",FACE,{"disambiguationData":[OSD([subQ6,subQ8,subQ9,subQ7,subQ4,subQ3,subQ2,subQ1,subQ0,subQ5,subQ10,subQ11])],"isStart":true})});}
            var sketch = newSketch(context, id + "F16", { "sketchPlane" : qUnion([Q0])});
            skLineSegment(sketch, "E79", {"start": v(0, 135) * mm, "end": v(0, 165) * mm, "construction": true});
            skCircle(sketch, "E80", {"center": v(0, 165) * mm, "radius": 6 * mm});
            skLineSegment(sketch, "E81", {"start": v(-80, 0) * mm, "end": v(80, 0) * mm, "construction": true});
            skLineSegment(sketch, "E82", {"start": v(0, 0) * mm, "end": v(0, 135) * mm, "construction": true});
            skLineSegment(sketch, "E83", {"start": v(0, 165) * mm, "end": v(-15, 165) * mm, "construction": true});
            skLineSegment(sketch, "E84.MirrorCS", {"start": v(0, 165) * mm, "end": v(15, 165) * mm, "construction": true});
            skArc(sketch, "E85", {"start": v(15, 165) * mm, "mid": v(0, 180.39) * mm, "end": v(-15, 165) * mm});
            skLineSegment(sketch, "E86", {"start": v(-15, 165) * mm, "end": v(-15, 153) * mm});
            skLineSegment(sketch, "E87", {"start": v(15, 165) * mm, "end": v(15, 153) * mm});
            skLineSegment(sketch, "E88", {"start": v(-15, 153) * mm, "end": v(-33, 135) * mm});
            skLineSegment(sketch, "E89.MirrorCS", {"start": v(15, 153) * mm, "end": v(33, 135) * mm});
            skLineSegment(sketch, "E90.MirrorCS", {"start": v(-15, -153) * mm, "end": v(-33, -135) * mm});
            skLineSegment(sketch, "E91.MirrorCS", {"start": v(-15, -165) * mm, "end": v(-15, -153) * mm});
            skArc(sketch, "E92.MirrorCS", {"start": v(15, -165) * mm, "mid": v(0, -180.39) * mm, "end": v(-15, -165) * mm});
            skCircle(sketch, "E93.MirrorC", {"center": v(0, -165) * mm, "radius": 6 * mm});
            skLineSegment(sketch, "E94.MirrorCS", {"start": v(15, -165) * mm, "end": v(15, -153) * mm});
            skLineSegment(sketch, "E95.MirrorCS", {"start": v(15, -153) * mm, "end": v(33, -135) * mm});
            skSolve(sketch);
        }
        {
            var Q0;
            Q0=makeQuery(id+"F16.imprint","IMPRINT",FACE,{"disambiguationData":[TD([[makeQuery(id+"F16.imprint","IMPRINT",EDGE,{"derivedFrom":sQuery(id+"F16.wireOp",EDGE,"E80")}),-1.0]])]});
            var Q1;
            {var subQ0=sQuery(id+"F16.wireOp",EDGE,"E90.MirrorCS");Q1=makeQuery(id+"F16.imprint","IMPRINT",FACE,{"disambiguationData":[TD([[makeQuery(id+"F16.imprint","IMPRINT",EDGE,{"derivedFrom":subQ0}),-1.0]])]});}
            var Q2;
            Q2=makeQuery(id+"F16.imprint","IMPRINT",FACE,{"disambiguationData":[TD([[makeQuery(id+"F16.imprint","IMPRINT",EDGE,{"derivedFrom":makeQuery(id+"F1.opExtrude","CAP_EDGE",EDGE,{"disambiguationData":[OSD([sQuery(id+"F0.wireOp",EDGE,"E1.left")])],"isStart":true})}),-1.0]])]});
            var Q3;
            Q3=makeQuery(id+"F2.opExtrude","CAP_FACE",FACE,{"disambiguationData":[OSD([sQuery(id+"F0.wireOp",EDGE,"E12"),sQuery(id+"F0.wireOp",EDGE,"E13"),sQuery(id+"F0.wireOp",EDGE,"E14"),sQuery(id+"F0.wireOp",EDGE,"E15"),sQuery(id+"F0.wireOp",EDGE,"E17.filletArc"),sQuery(id+"F0.wireOp",EDGE,"E18.filletArc"),sQuery(id+"F0.wireOp",EDGE,"E19.filletArc"),sQuery(id+"F0.wireOp",EDGE,"E20.filletArc"),sQuery(id+"F0.wireOp",EDGE,"E25.0"),sQuery(id+"F0.wireOp",EDGE,"E25.1"),sQuery(id+"F0.wireOp",EDGE,"E25.2"),sQuery(id+"F0.wireOp",EDGE,"E25.3"),sQuery(id+"F0.wireOp",EDGE,"E25.4"),sQuery(id+"F0.wireOp",EDGE,"E25.5"),sQuery(id+"F0.wireOp",EDGE,"E25.6"),sQuery(id+"F0.wireOp",EDGE,"E25.7")])],"isStart":false});
            extrude(context, id + "F17", {"entities" : qUnion([Q0, Q1, Q2]), "endBound" : BoundingType.UP_TO_SURFACE, "endBoundEntityFace" : qUnion([Q3]), "depth" : 25 * mm});
        }
    });
